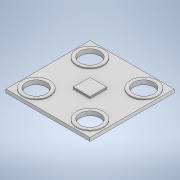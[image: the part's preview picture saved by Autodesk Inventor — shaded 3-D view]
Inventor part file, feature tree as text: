
AUTODESK INVENTOR PART (.ipt)
format: ipt  version: 2020 (Build 240168000, 168)  size: 164,864 bytes
history: native  units: mm
features: sketch x7, hole x4, extrude x3
ambient origin geometry x8: Origin, YZ Plane, XZ Plane, XY Plane, X Axis, Y Axis, Z Axis, Center Point
bodies: Solid1 (feature_tree)
feature tree (14):
  extrude  "Extrusion1"  Depth=25.0mm
  extrude  "Extrusion2"  Depth=6.0mm
  extrude  "Extrusion4"  Depth=6.0mm
  hole  "Hole2"  [1 undecoded]
  hole  "Hole3"  [1 undecoded]
  hole  "Hole4"  [1 undecoded]
  hole  "Hole5"  [1 undecoded]
  sketch  "Sketch1"  dims[d0=25.0mm d1=25.0mm]
  sketch  "Sketch2"  dims[d8=6.0mm d9=6.0mm]
  sketch  "Sketch6"  dims[d10=6.0mm d11=6.0mm]
  sketch  "Sketch7"  dims[d16=1.0mm d17=0.0mm d18=2.5mm]
  sketch  "Sketch8"  dims[d19=2.5mm d20=2.5mm]
  sketch  "Sketch9"  dims[d21=2.5mm d22=2.5mm]
  sketch  "Sketch10"  dims[d23=2.5mm d24=0.5mm d25=0.0mm d43=8.0mm d44=8.0mm d45=8.0mm d46=8.0mm d47=0.25mm d48=0.0mm d49=6.0mm d50=6.0mm d51=6.0mm d52=4.0mm d53=2.0mm d54=90.0deg d55=1.25mm d56=0.0mm d57=6.0mm d58=6.0mm d59=6.0mm d60=4.0mm d61=2.0mm d62=90.0deg d63=1.25mm d64=0.0mm d65=6.0mm d66=6.0mm d67=6.0mm d68=4.0mm d69=2.0mm d70=90.0deg d71=1.25mm d72=0.0mm d73=6.0mm d74=6.0mm d75=6.0mm d76=4.0mm d77=2.0mm d78=90.0deg d79=1.25mm d80=0.0mm]
note: 4 required parameter values undecoded (feature->parameter linkage not recoverable at this tier; creation-order binding heuristic only, values carry confidence <= 0.55)
